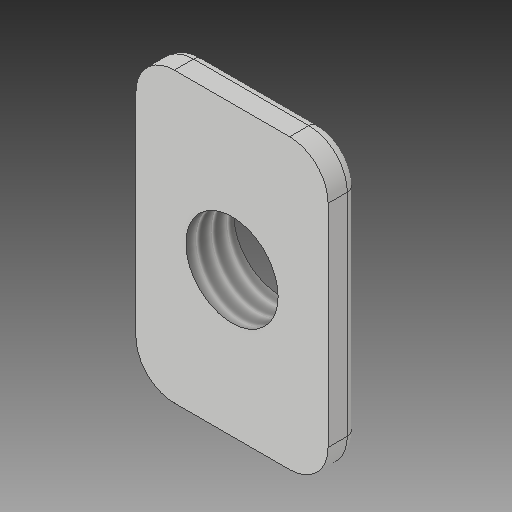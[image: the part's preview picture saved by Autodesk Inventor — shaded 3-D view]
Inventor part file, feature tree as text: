
AUTODESK INVENTOR PART (.ipt)
format: ipt  version: 2018 (Build 220112000, 112)  size: 145,920 bytes
history: native  units: mm
features: other x3, sketch x2
ambient origin geometry x8: Origin, YZ Plane, XZ Plane, XY Plane, X Axis, Y Axis, Z Axis, Center Point
bodies: Solid1 (feature_tree)
feature tree (5):
  other  "M5 Tee Nut.ipt"
  other  "Solid1::M5 Tee Nut.ipt"
  other  "TaggingFeature1"
  sketch  "Sketch1"  dims[d0=10.0mm]
  sketch  "Sketch2"
